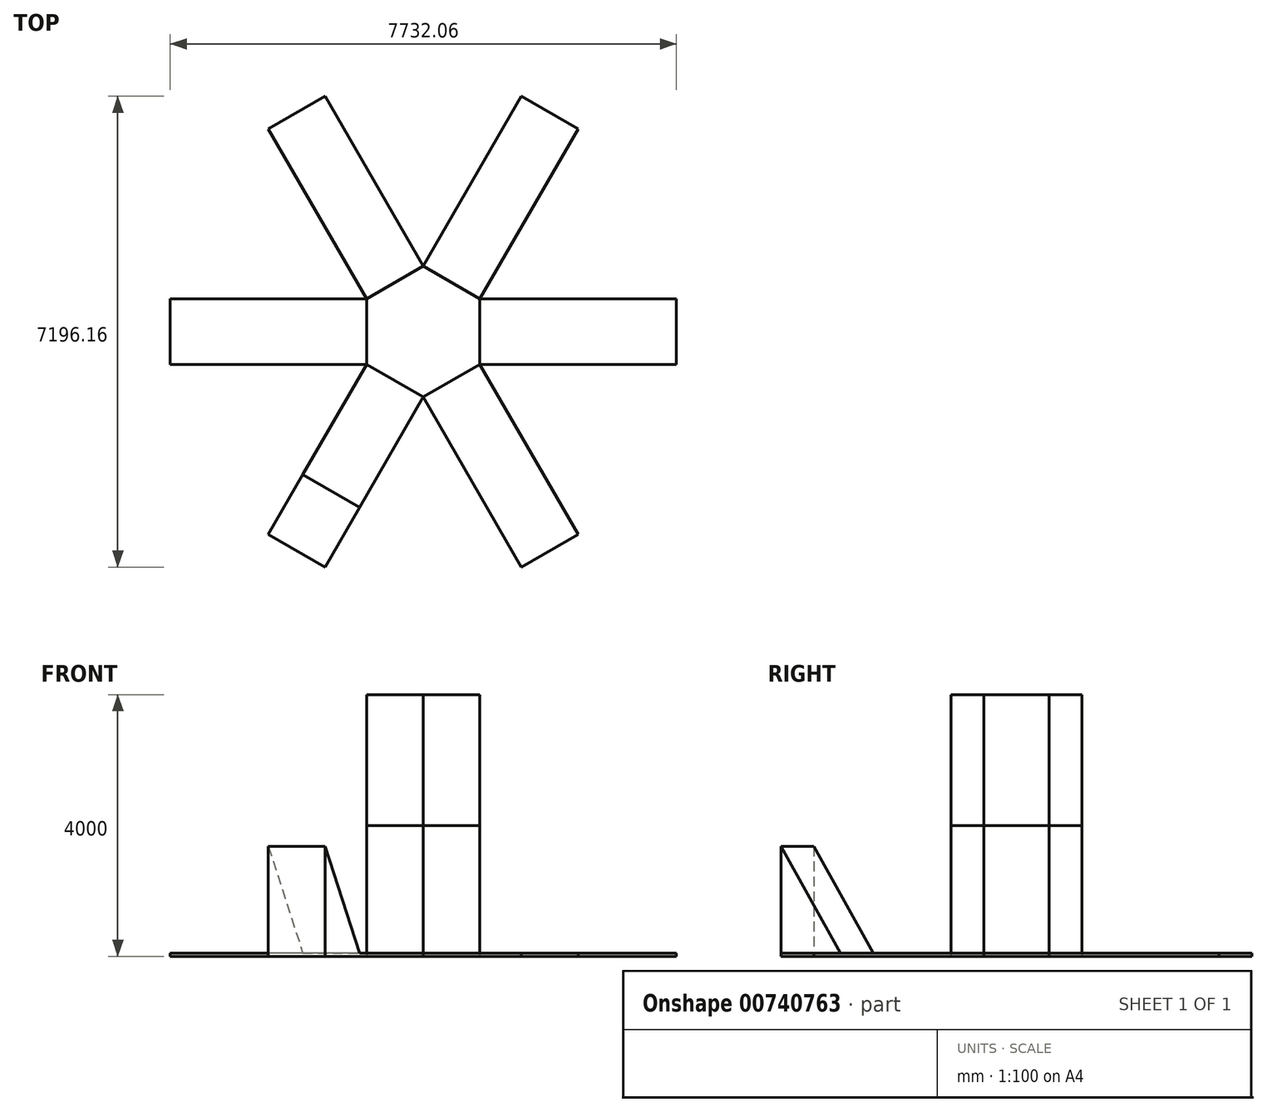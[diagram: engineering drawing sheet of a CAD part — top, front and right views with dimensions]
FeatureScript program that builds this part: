
annotation { "Feature Type Name" : "Feature", "Feature Type Description" : "" }
export const myFeature = defineFeature(function(context is Context, id is Id, definition is map)
    precondition{}
    {
        {
            var Q0;
            Q0=qCreatedBy(makeId("Top.planeOp"),FACE);
            var sketch = newSketch(context, id + "F0", { "sketchPlane" : qUnion([Q0])});
            skCircle(sketch, "E0.cCircle", {"center": v(0, 0) * mm, "radius": 866.03 * mm, "construction": true});
            skLineSegment(sketch, "E0.0", {"start": v(-866.03, -500) * mm, "end": v(-866.03, 500) * mm});
            skLineSegment(sketch, "E0.1", {"start": v(-866.03, 500) * mm, "end": v(0, 1000) * mm});
            skLineSegment(sketch, "E0.2", {"start": v(0, 1000) * mm, "end": v(866.03, 500) * mm});
            skLineSegment(sketch, "E0.3", {"start": v(866.03, 500) * mm, "end": v(866.03, -500) * mm});
            skLineSegment(sketch, "E0.4", {"start": v(866.03, -500) * mm, "end": v(0, -1000) * mm});
            skLineSegment(sketch, "E0.5", {"start": v(0, -1000) * mm, "end": v(-866.03, -500) * mm});
            skPoint(sketch, "E0.0.midPoint", {"position": v(-866.03, 0) * mm});
            skLineSegment(sketch, "E1.bottom", {"start": v(-866.03, 500) * mm, "end": v(-2866.03, 500) * mm});
            skLineSegment(sketch, "E1.top", {"start": v(-866.03, -500) * mm, "end": v(-2866.03, -500) * mm});
            skLineSegment(sketch, "E1.left", {"start": v(-866.03, 500) * mm, "end": v(-866.03, -500) * mm});
            skLineSegment(sketch, "E1.right", {"start": v(-2866.03, 500) * mm, "end": v(-2866.03, -500) * mm});
            skLineSegment(sketch, "E2.1.0", {"start": v(-866.03, -500) * mm, "end": v(-1866.03, -2232.05) * mm});
            skLineSegment(sketch, "E2.1.1", {"start": v(-1866.03, -2232.05) * mm, "end": v(-1000, -2732.05) * mm});
            skLineSegment(sketch, "E2.1.2", {"start": v(0, -1000) * mm, "end": v(-1000, -2732.05) * mm});
            skLineSegment(sketch, "E2.2.0", {"start": v(0, -1000) * mm, "end": v(1000, -2732.05) * mm});
            skLineSegment(sketch, "E2.2.1", {"start": v(1000, -2732.05) * mm, "end": v(1866.03, -2232.05) * mm});
            skLineSegment(sketch, "E2.2.2", {"start": v(866.03, -500) * mm, "end": v(1866.03, -2232.05) * mm});
            skLineSegment(sketch, "E2.3.0", {"start": v(866.03, -500) * mm, "end": v(2866.03, -500) * mm});
            skLineSegment(sketch, "E2.3.1", {"start": v(2866.03, -500) * mm, "end": v(2866.03, 500) * mm});
            skLineSegment(sketch, "E2.3.2", {"start": v(866.03, 500) * mm, "end": v(2866.03, 500) * mm});
            skLineSegment(sketch, "E2.4.0", {"start": v(866.03, 500) * mm, "end": v(1866.03, 2232.05) * mm});
            skLineSegment(sketch, "E2.4.1", {"start": v(1866.03, 2232.05) * mm, "end": v(1000, 2732.05) * mm});
            skLineSegment(sketch, "E2.4.2", {"start": v(0, 1000) * mm, "end": v(1000, 2732.05) * mm});
            skLineSegment(sketch, "E2.5.0", {"start": v(0, 1000) * mm, "end": v(-1000, 2732.05) * mm});
            skLineSegment(sketch, "E2.5.1", {"start": v(-1000, 2732.05) * mm, "end": v(-1866.03, 2232.05) * mm});
            skLineSegment(sketch, "E2.5.2", {"start": v(-866.03, 500) * mm, "end": v(-1866.03, 2232.05) * mm});
            skLineSegment(sketch, "E3.bottom", {"start": v(-2866.03, 500) * mm, "end": v(-3866.03, 500) * mm});
            skLineSegment(sketch, "E3.top", {"start": v(-2866.03, -500) * mm, "end": v(-3866.03, -500) * mm});
            skLineSegment(sketch, "E3.right", {"start": v(-3866.03, 500) * mm, "end": v(-3866.03, -500) * mm});
            skLineSegment(sketch, "E4.1.0", {"start": v(-1866.03, -2232.05) * mm, "end": v(-2366.03, -3098.08) * mm});
            skLineSegment(sketch, "E4.1.1", {"start": v(-2366.03, -3098.08) * mm, "end": v(-1500, -3598.08) * mm});
            skLineSegment(sketch, "E4.1.2", {"start": v(-1000, -2732.05) * mm, "end": v(-1500, -3598.08) * mm});
            skLineSegment(sketch, "E4.2.0", {"start": v(1000, -2732.05) * mm, "end": v(1500, -3598.08) * mm});
            skLineSegment(sketch, "E4.2.1", {"start": v(1500, -3598.08) * mm, "end": v(2366.03, -3098.08) * mm});
            skLineSegment(sketch, "E4.2.2", {"start": v(1866.03, -2232.05) * mm, "end": v(2366.03, -3098.08) * mm});
            skLineSegment(sketch, "E4.3.0", {"start": v(2866.03, -500) * mm, "end": v(3866.03, -500) * mm});
            skLineSegment(sketch, "E4.3.1", {"start": v(3866.03, -500) * mm, "end": v(3866.03, 500) * mm});
            skLineSegment(sketch, "E4.3.2", {"start": v(2866.03, 500) * mm, "end": v(3866.03, 500) * mm});
            skLineSegment(sketch, "E4.4.0", {"start": v(1866.03, 2232.05) * mm, "end": v(2366.03, 3098.08) * mm});
            skLineSegment(sketch, "E4.4.1", {"start": v(2366.03, 3098.08) * mm, "end": v(1500, 3598.08) * mm});
            skLineSegment(sketch, "E4.4.2", {"start": v(1000, 2732.05) * mm, "end": v(1500, 3598.08) * mm});
            skLineSegment(sketch, "E4.5.0", {"start": v(-1000, 2732.05) * mm, "end": v(-1500, 3598.08) * mm});
            skLineSegment(sketch, "E4.5.1", {"start": v(-1500, 3598.08) * mm, "end": v(-2366.03, 3098.08) * mm});
            skLineSegment(sketch, "E4.5.2", {"start": v(-1866.03, 2232.05) * mm, "end": v(-2366.03, 3098.08) * mm});
            skLineSegment(sketch, "E5", {"start": v(0, 0) * mm, "end": v(-1933.01, -3348.08) * mm});
            skSolve(sketch);
        }
        {
            var Q0;
            Q0=makeQuery(id+"F0.imprint","IMPRINT",FACE,{"disambiguationData":[TD([[makeQuery(id+"F0.imprint","IMPRINT",EDGE,{"derivedFrom":sQuery(id+"F0.wireOp",EDGE,"E0.1")}),-1.0]])]});
            extrude(context, id + "F1", {"entities" : qUnion([Q0]), "depth" : 2000 * mm, "offsetDistance" : 25.4 * mm});
        }
        {
            var Q0;
            Q0 = qSketchRegion(id + "F0", true);
            extrude(context, id + "F2", {"entities" : qUnion([Q0]), "operationType" : NewBodyOperationType.ADD, "depth" : 50.8 * mm, "offsetDistance" : 25.4 * mm});
        }
        {
            var Q0;
            Q0=makeQuery(id+"F1.opExtrude","CAP_FACE",FACE,{"disambiguationData":[OSD([sQuery(id+"F0.wireOp",EDGE,"E0.1"),sQuery(id+"F0.wireOp",EDGE,"E0.2"),sQuery(id+"F0.wireOp",EDGE,"E0.3"),sQuery(id+"F0.wireOp",EDGE,"E0.4"),sQuery(id+"F0.wireOp",EDGE,"E0.5"),sQuery(id+"F0.wireOp",EDGE,"E1.left")])],"isStart":false});
            extrude(context, id + "F3", {"entities" : qUnion([Q0]), "depth" : 2000 * mm, "offsetDistance" : 25 * mm});
        }
        {
            var Q0;
            Q0=makeQuery(id+"F2.opExtrude","SWEPT_FACE",FACE,{"disambiguationData":[OSD([sQuery(id+"F0.wireOp",EDGE,"E2.1.2"),sQuery(id+"F0.wireOp",EDGE,"E4.1.2")])]});
            var sketch = newSketch(context, id + "F4", { "sketchPlane" : qUnion([Q0])});
            skLineSegment(sketch, "E6", {"start": v(-3866.03, 50.8) * mm, "end": v(-3866.03, 1679.86) * mm});
            skLineSegment(sketch, "E7", {"start": v(-3866.03, 1679.86) * mm, "end": v(-2780.63, 0) * mm});
            skLineSegment(sketch, "E8.bottom", {"start": v(-705.75, 4000) * mm, "end": v(1294.25, 4000) * mm});
            skLineSegment(sketch, "E8.top", {"start": v(-705.75, 5000) * mm, "end": v(1294.25, 5000) * mm});
            skLineSegment(sketch, "E8.left", {"start": v(-705.75, 4000) * mm, "end": v(-705.75, 5000) * mm});
            skLineSegment(sketch, "E8.right", {"start": v(1294.25, 4000) * mm, "end": v(1294.25, 5000) * mm});
            skArc(sketch, "E9", {"start": v(-705.75, 4000) * mm, "mid": v(294.25, 5000) * mm, "end": v(1294.25, 4000) * mm});
            skLineSegment(sketch, "E10", {"start": v(1294.25, 4000) * mm, "end": v(1294.25, 0) * mm});
            skSolve(sketch);
        }
        {
            var Q0;
            {var subQ0=sQuery(id+"F4.wireOp",EDGE,"E6");Q0=makeQuery(id+"F4.imprint","IMPRINT",FACE,{"disambiguationData":[TD([[makeQuery(id+"F4.imprint","IMPRINT",EDGE,{"derivedFrom":subQ0}),-1.0]])]});}
            extrude(context, id + "F5", {"entities" : qUnion([Q0]), "operationType" : NewBodyOperationType.ADD, "oppositeDirection" : true, "depth" : 1000 * mm, "offsetDistance" : 25 * mm});
        }
    });
